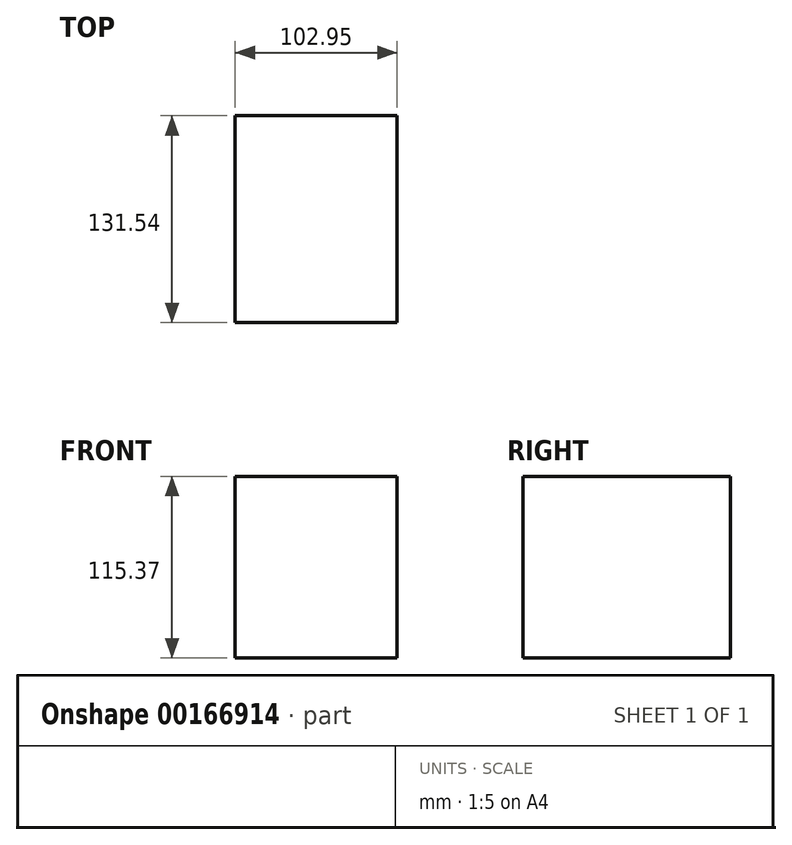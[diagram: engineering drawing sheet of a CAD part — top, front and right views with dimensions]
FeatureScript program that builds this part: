
annotation { "Feature Type Name" : "Feature", "Feature Type Description" : "" }
export const myFeature = defineFeature(function(context is Context, id is Id, definition is map)
    precondition{}
    {
        {
            var Q0;
            Q0=qCreatedBy(makeId("Front.planeOp"),FACE);
            var sketch = newSketch(context, id + "F0", { "sketchPlane" : qUnion([Q0])});
            skLineSegment(sketch, "E0.bottom", {"start": v(0, 0) * mm, "end": v(102.95, 0) * mm});
            skLineSegment(sketch, "E0.top", {"start": v(0, 115.37) * mm, "end": v(102.95, 115.37) * mm});
            skLineSegment(sketch, "E0.left", {"start": v(0, 0) * mm, "end": v(0, 115.37) * mm});
            skLineSegment(sketch, "E0.right", {"start": v(102.95, 0) * mm, "end": v(102.95, 115.37) * mm});
            skSolve(sketch);
        }
        {
            var Q0;
            Q0 = qSketchRegion(id + "F0", true);
            extrude(context, id + "F1", {"entities" : qUnion([Q0]), "depth" : 131.54 * mm});
        }
    });
